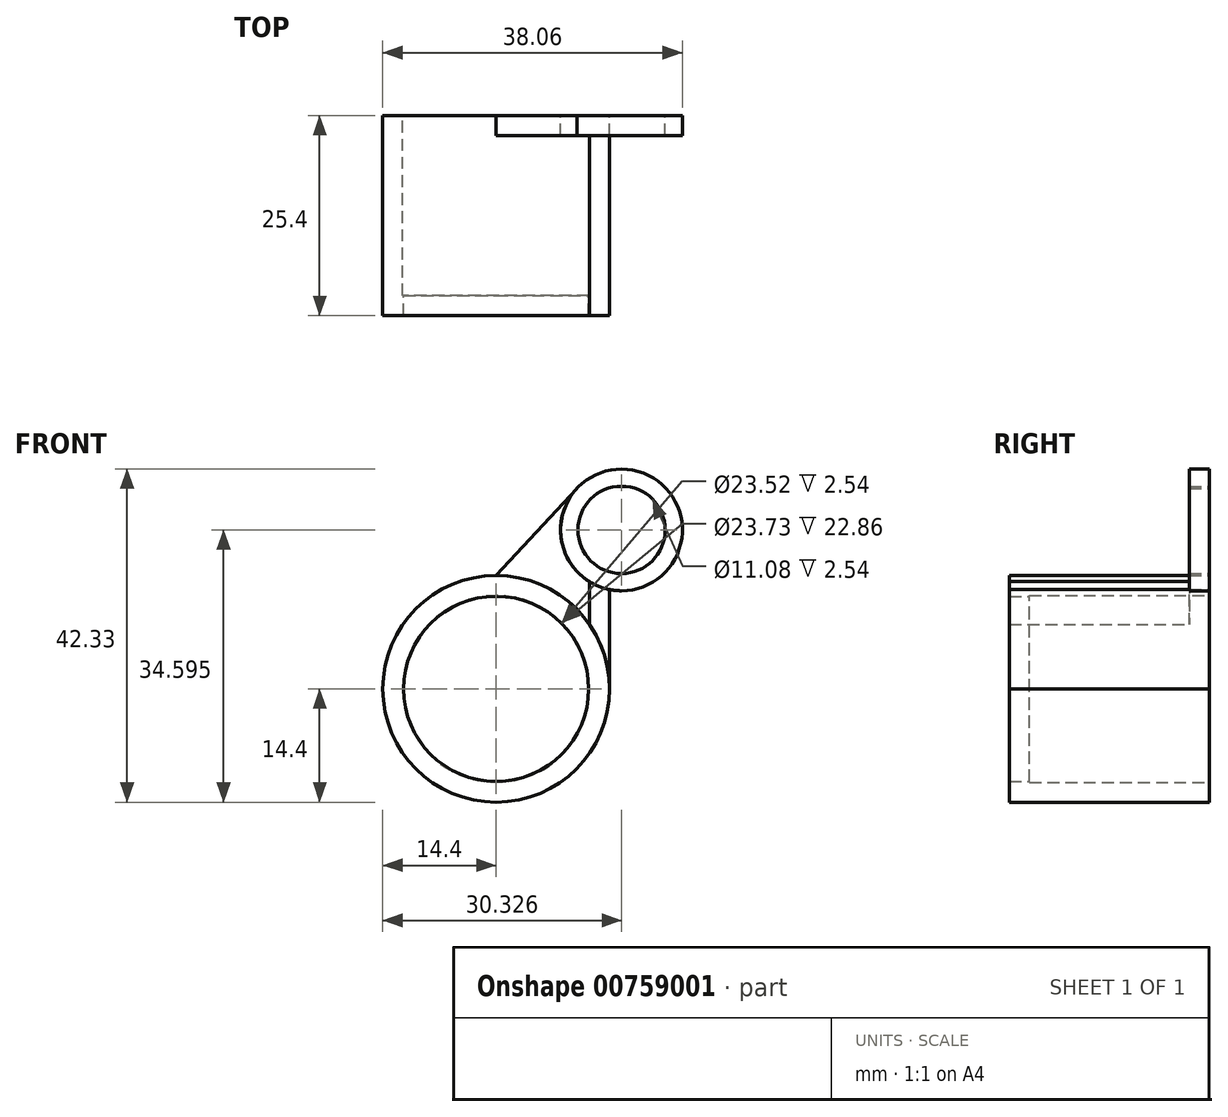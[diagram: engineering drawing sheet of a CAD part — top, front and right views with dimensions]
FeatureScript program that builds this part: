
annotation { "Feature Type Name" : "Feature", "Feature Type Description" : "" }
export const myFeature = defineFeature(function(context is Context, id is Id, definition is map)
    precondition{}
    {
        {
            var Q0;
            Q0=qCreatedBy(makeId("Front.planeOp"),FACE);
            var sketch = newSketch(context, id + "F0", { "sketchPlane" : qUnion([Q0])});
            skCircle(sketch, "E0", {"center": v(0, 0) * mm, "radius": 14.4 * mm});
            skCircle(sketch, "E1", {"center": v(0, 0) * mm, "radius": 11.76 * mm});
            skCircle(sketch, "E2", {"center": v(15.93, 20.2) * mm, "radius": 7.73 * mm});
            skLineSegment(sketch, "E3", {"start": v(0, 14.4) * mm, "end": v(10.26, 25.45) * mm});
            skLineSegment(sketch, "E4", {"start": v(14.4, 12.62) * mm, "end": v(14.4, 0) * mm});
            skCircle(sketch, "E5", {"center": v(15.93, 20.2) * mm, "radius": 5.54 * mm});
            skSolve(sketch);
        }
        {
            var Q0;
            Q0=makeQuery(id+"F0.imprint","IMPRINT",FACE,{"disambiguationData":[TD([[makeQuery(id+"F0.imprint","IMPRINT",EDGE,{"derivedFrom":sQuery(id+"F0.wireOp",EDGE,"E1")}),-1.0]])]});
            var Q1;
            Q1=makeQuery(id+"F0.imprint","IMPRINT",FACE,{"disambiguationData":[TD([[makeQuery(id+"F0.imprint","IMPRINT",EDGE,{"derivedFrom":sQuery(id+"F0.wireOp",EDGE,"E5")}),-1.0]])]});
            extrude(context, id + "F1", {"entities" : qUnion([Q0, Q1]), "depth" : 25.4 * mm, "offsetDistance" : 25.4 * mm});
        }
        {
            var Q0;
            {var subQ0=sQuery(id+"F0.wireOp",EDGE,"E3");Q0=makeQuery(id+"F0.imprint","IMPRINT",FACE,{"disambiguationData":[TD([[makeQuery(id+"F0.imprint","IMPRINT",EDGE,{"derivedFrom":subQ0}),-1.0]])]});}
            extrude(context, id + "F2", {"entities" : qUnion([Q0]), "depth" : 25.4 * mm, "offsetDistance" : 25.4 * mm});
        }
        {
            var Q0;
            Q0=makeQuery(id+"F1.opExtrude","SWEPT_FACE",FACE,{"disambiguationData":[OSD([sQuery(id+"F0.wireOp",EDGE,"E2")])]});
            var Q1;
            Q1=makeQuery(id+"F1.opExtrude","SWEPT_FACE",FACE,{"disambiguationData":[OSD([sQuery(id+"F0.wireOp",EDGE,"E5")])]});
            var Q2;
            Q2=makeQuery(id+"F1.opExtrude","SWEPT_FACE",FACE,{"disambiguationData":[OSD([sQuery(id+"F0.wireOp",EDGE,"E1")])]});
            var Q3;
            Q3=makeQuery(id+"F2.opExtrude","SWEPT_FACE",FACE,{"disambiguationData":[OSD([sQuery(id+"F0.wireOp",EDGE,"E0")])]});
            var Q4;
            Q4=makeQuery(id+"F2.opExtrude","SWEPT_FACE",FACE,{"disambiguationData":[OSD([sQuery(id+"F0.wireOp",EDGE,"E2")])]});
            var Q5;
            Q5=makeQuery(id+"F1.opExtrude","CAP_FACE",FACE,{"disambiguationData":[OSD([sQuery(id+"F0.wireOp",EDGE,"E0"),sQuery(id+"F0.wireOp",EDGE,"E1")])],"isStart":true});
            var Q6;
            Q6=makeQuery(id+"F2.opExtrude","CAP_FACE",FACE,{"disambiguationData":[OSD([sQuery(id+"F0.wireOp",EDGE,"E0"),sQuery(id+"F0.wireOp",EDGE,"E2"),sQuery(id+"F0.wireOp",EDGE,"E3"),sQuery(id+"F0.wireOp",EDGE,"E4")])],"isStart":false});
            var Q7;
            Q7=makeQuery(id+"F1.opExtrude","CAP_FACE",FACE,{"disambiguationData":[OSD([sQuery(id+"F0.wireOp",EDGE,"E2"),sQuery(id+"F0.wireOp",EDGE,"E5")])],"isStart":false});
            var Q8;
            Q8=makeQuery(id+"F2.opExtrude","SWEPT_FACE",FACE,{"disambiguationData":[OSD([sQuery(id+"F0.wireOp",EDGE,"E3")])]});
            shell(context, id + "F3", {"entities" : qUnion([Q0, Q1, Q2, Q3, Q4, Q5, Q6, Q7, Q8]), "thickness" : 2.54 * mm});
        }
    });
